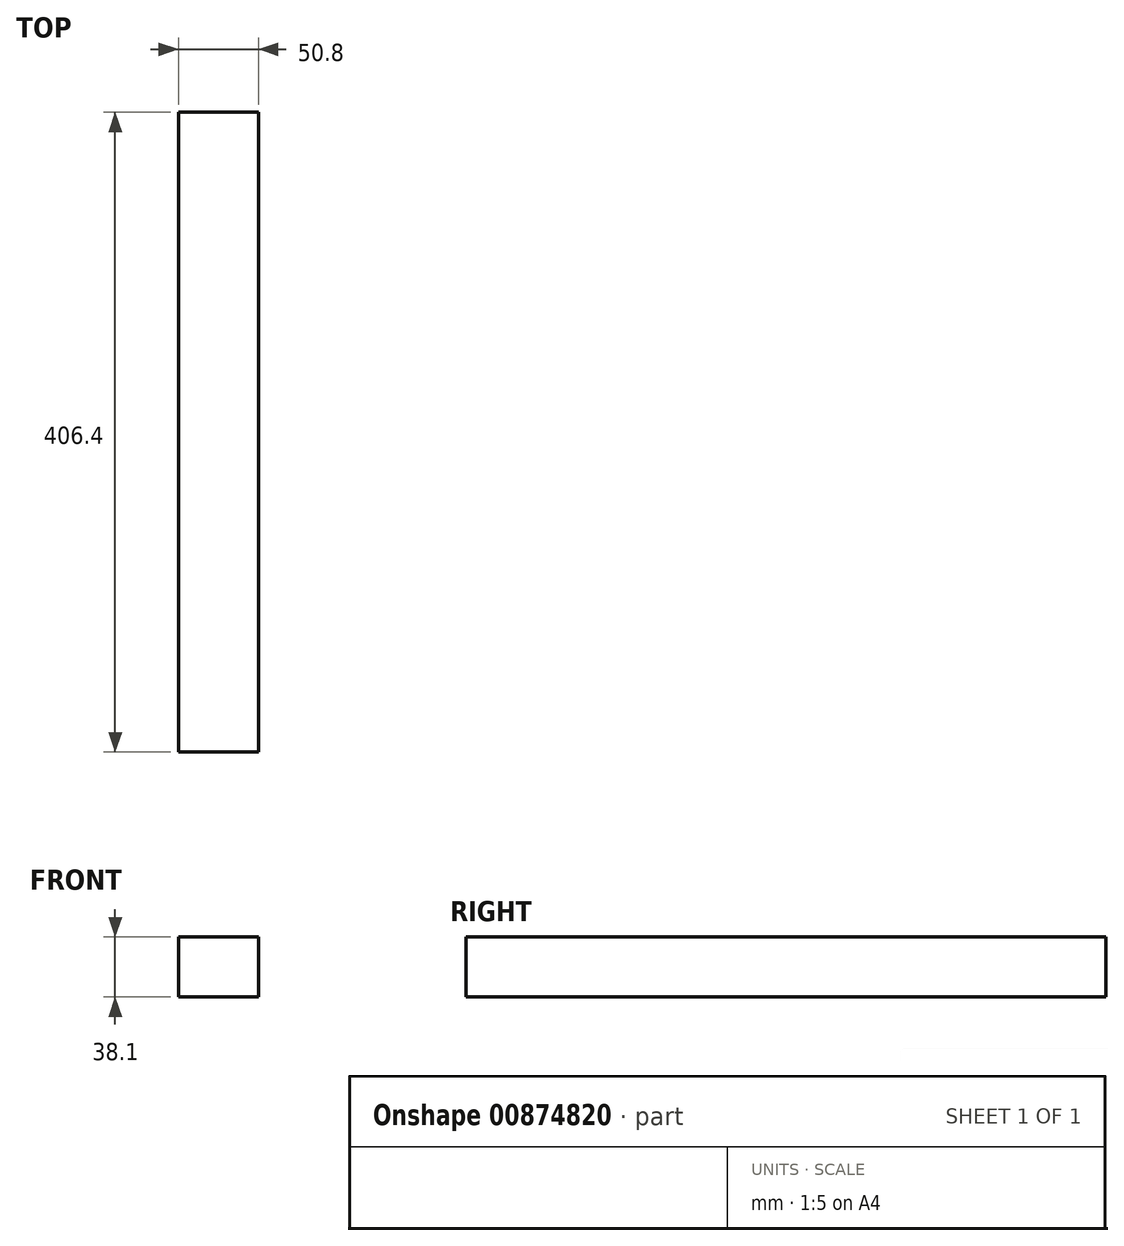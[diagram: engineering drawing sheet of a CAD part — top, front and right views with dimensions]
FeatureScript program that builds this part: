
annotation { "Feature Type Name" : "Feature", "Feature Type Description" : "" }
export const myFeature = defineFeature(function(context is Context, id is Id, definition is map)
    precondition{}
    {
        {
            var Q0;
            Q0=qCreatedBy(makeId("Front.planeOp"),FACE);
            var sketch = newSketch(context, id + "F0", { "sketchPlane" : qUnion([Q0])});
            skLineSegment(sketch, "E0.bottom", {"start": v(-23.7, 28.25) * mm, "end": v(27.1, 28.25) * mm});
            skLineSegment(sketch, "E0.top", {"start": v(-23.7, -9.85) * mm, "end": v(27.1, -9.85) * mm});
            skLineSegment(sketch, "E0.left", {"start": v(-23.7, 28.25) * mm, "end": v(-23.7, -9.85) * mm});
            skLineSegment(sketch, "E0.right", {"start": v(27.1, 28.25) * mm, "end": v(27.1, -9.85) * mm});
            skSolve(sketch);
        }
        {
            var Q0;
            Q0 = qSketchRegion(id + "F0", true);
            extrude(context, id + "F1", {"entities" : qUnion([Q0]), "depth" : 406.4 * mm, "offsetDistance" : 25.4 * mm});
        }
    });
